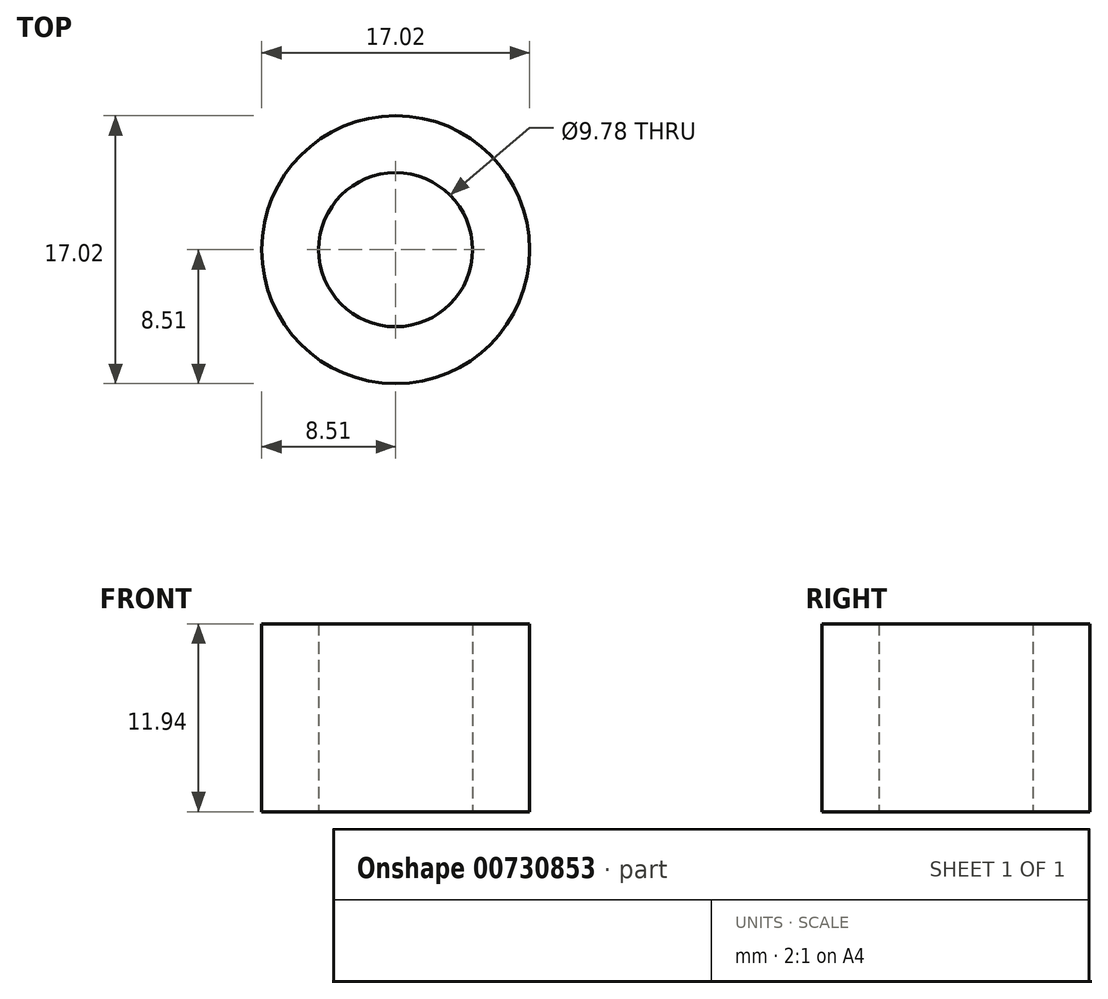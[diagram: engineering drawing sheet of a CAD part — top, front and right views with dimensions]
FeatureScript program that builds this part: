
annotation { "Feature Type Name" : "Feature", "Feature Type Description" : "" }
export const myFeature = defineFeature(function(context is Context, id is Id, definition is map)
    precondition{}
    {
        {
            var Q0;
            Q0=qCreatedBy(makeId("Top.planeOp"),FACE);
            var sketch = newSketch(context, id + "F0", { "sketchPlane" : qUnion([Q0])});
            skCircle(sketch, "E0", {"center": v(0, 0) * mm, "radius": 8.5 * mm});
            skCircle(sketch, "E1", {"center": v(0, 0) * mm, "radius": 4.89 * mm});
            skSolve(sketch);
        }
        {
            var Q0;
            Q0 = qSketchRegion(id + "F0", true);
            extrude(context, id + "F1", {"entities" : qUnion([Q0]), "depth" : 11.94 * mm, "offsetDistance" : 25.4 * mm});
        }
    });
